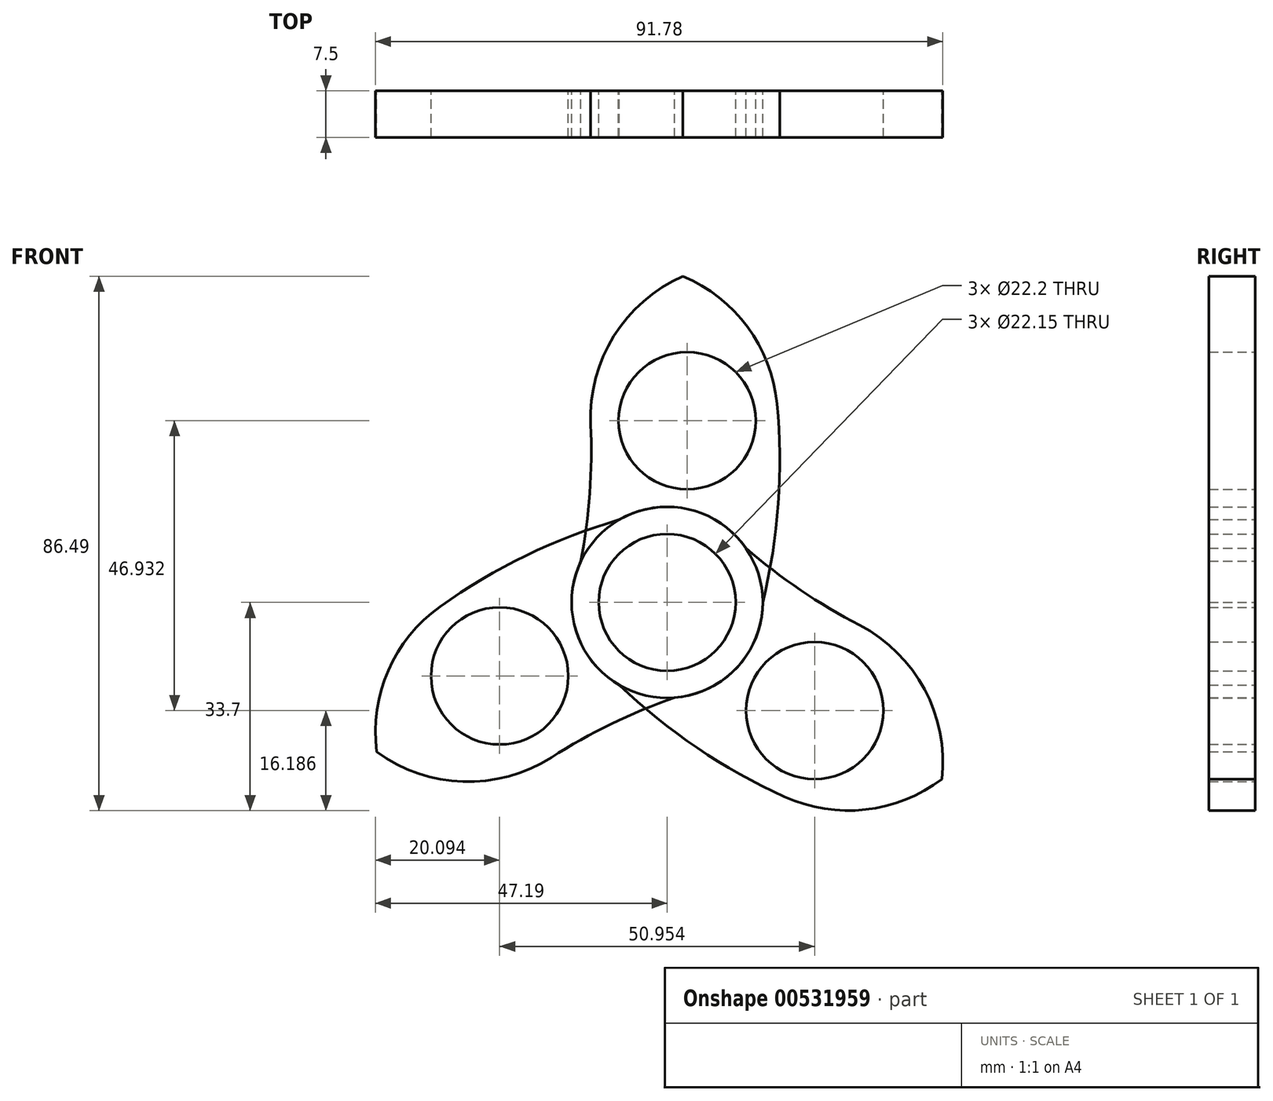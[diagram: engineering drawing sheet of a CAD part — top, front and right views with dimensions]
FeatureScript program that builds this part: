
annotation { "Feature Type Name" : "Feature", "Feature Type Description" : "" }
export const myFeature = defineFeature(function(context is Context, id is Id, definition is map)
    precondition{}
    {
        {
            var Q0;
            Q0=qCreatedBy(makeId("Front.planeOp"),FACE);
            var sketch = newSketch(context, id + "F0", { "sketchPlane" : qUnion([Q0])});
            skCircle(sketch, "E0", {"center": v(0, 0) * mm, "radius": 11.08 * mm});
            skCircle(sketch, "E1", {"center": v(0, 0) * mm, "radius": 15.46 * mm});
            skArc(sketch, "E2", {"start": v(-15.46, 0) * mm, "mid": v(-12.31, 27.45) * mm, "end": v(-17.1, 54.66) * mm});
            skArc(sketch, "E3", {"start": v(15.46, 0) * mm, "mid": v(18.1, 27.65) * mm, "end": v(12.71, 54.9) * mm});
            skLineSegment(sketch, "E4", {"start": v(-17.1, 54.66) * mm, "end": v(12.71, 54.9) * mm});
            skCircle(sketch, "E5", {"center": v(3.24, 29.42) * mm, "radius": 11.1 * mm});
            skSolve(sketch);
        }
        {
            var Q0;
            Q0 = qSketchRegion(id + "F0", true);
            extrude(context, id + "F1", {"entities" : qUnion([Q0]), "depth" : 7.5 * mm, "offsetDistance" : 25 * mm});
        }
        {
            var Q0;
            Q0=makeQuery(id+"F1.opExtrude","SWEPT_EDGE",EDGE,{"disambiguationData":[OSD([sQuery(id+"F0.wireOp",EDGE,"E3"),sQuery(id+"F0.wireOp",EDGE,"E4")])]});
            var Q1;
            Q1=makeQuery(id+"F1.opExtrude","SWEPT_EDGE",EDGE,{"disambiguationData":[OSD([sQuery(id+"F0.wireOp",EDGE,"E2"),sQuery(id+"F0.wireOp",EDGE,"E4")])]});
            fillet(context, id + "F2", {"entities" : qUnion([Q0, Q1]), "radius" : 25 * mm, "tangentPropagation" : true, "allowEdgeOverflow" : false});
        }
        {
            var Q0;
            Q0=makeQuery(id+"F1.opExtrude","SWEPT_BODY",BODY,{"disambiguationData":[OSD([sQuery(id+"F0.wireOp",EDGE,"E0"),sQuery(id+"F0.wireOp",EDGE,"E1"),sQuery(id+"F0.wireOp",EDGE,"E2"),sQuery(id+"F0.wireOp",EDGE,"E3"),sQuery(id+"F0.wireOp",EDGE,"E4"),sQuery(id+"F0.wireOp",EDGE,"E5")])]});
            var Q1;
            Q1=makeQuery(id+"F1.opExtrude","CAP_EDGE",EDGE,{"disambiguationData":[OSD([sQuery(id+"F0.wireOp",EDGE,"E0")])],"isStart":false});
            transform(context, id + "F3", {"entities" : qUnion([Q0]), "transformType" : TransformType.ROTATION, "transformAxis" : qUnion([Q1]), "angle" : 120 * degree, "makeCopy" : true});
        }
        {
            var Q0;
            Q0=makeQuery(id+"F3.opPattern","COPY",BODY,{"derivedFrom":makeQuery(id+"F1.opExtrude","SWEPT_BODY",BODY,{"disambiguationData":[OSD([sQuery(id+"F0.wireOp",EDGE,"E0"),sQuery(id+"F0.wireOp",EDGE,"E1"),sQuery(id+"F0.wireOp",EDGE,"E2"),sQuery(id+"F0.wireOp",EDGE,"E3"),sQuery(id+"F0.wireOp",EDGE,"E4"),sQuery(id+"F0.wireOp",EDGE,"E5")])]}),"instanceName":"1"});
            var Q1;
            Q1=makeQuery(id+"F1.opExtrude","CAP_EDGE",EDGE,{"disambiguationData":[OSD([sQuery(id+"F0.wireOp",EDGE,"E0")])],"isStart":false});
            transform(context, id + "F4", {"entities" : qUnion([Q0]), "transformType" : TransformType.ROTATION, "transformAxis" : qUnion([Q1]), "angle" : 120 * degree, "makeCopy" : true});
        }
    });
